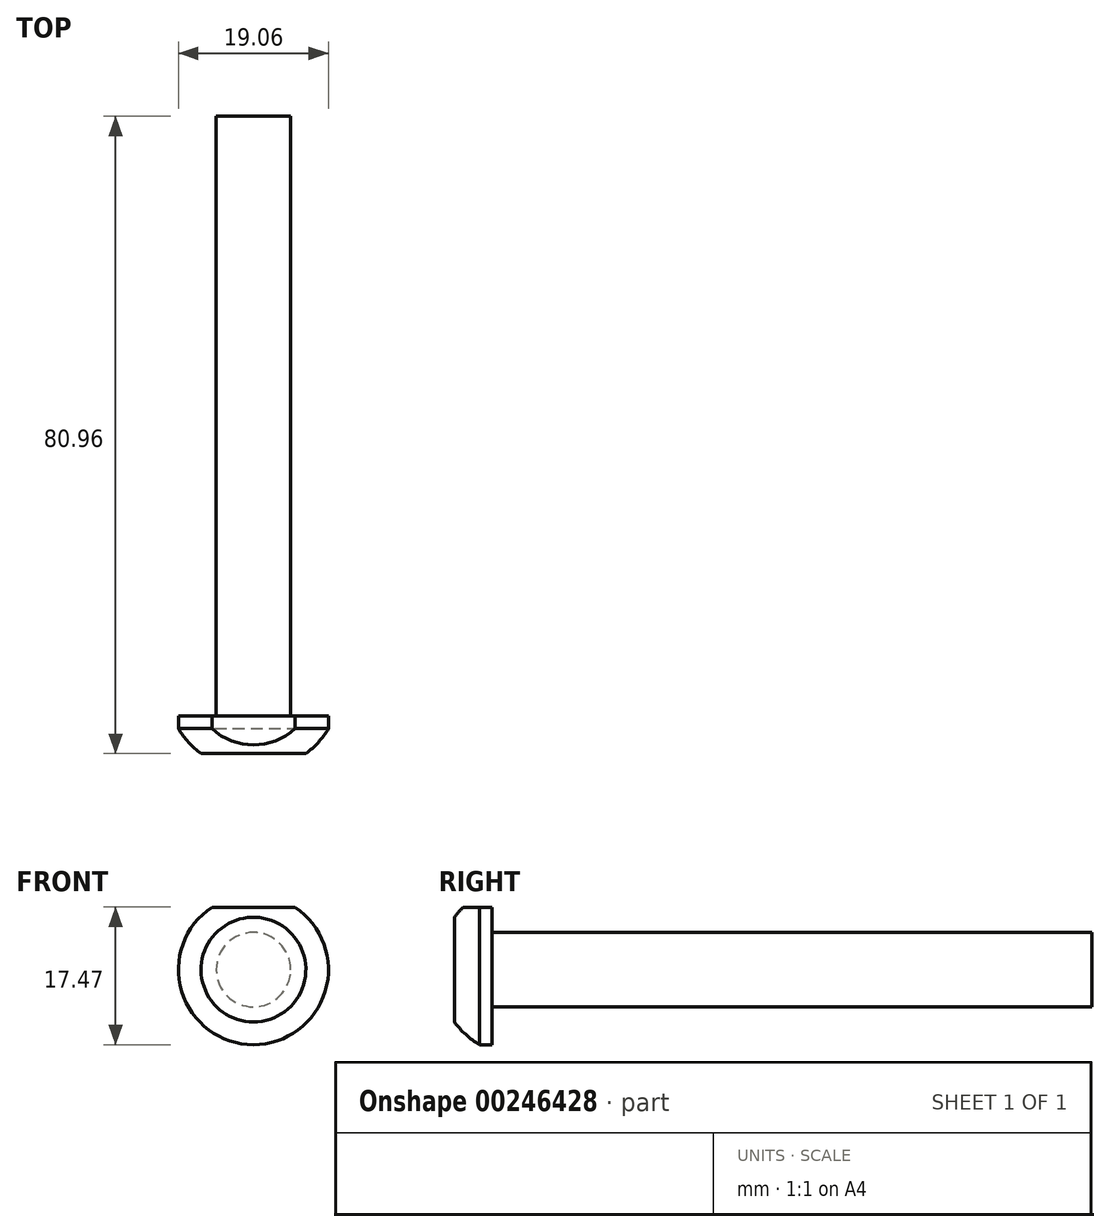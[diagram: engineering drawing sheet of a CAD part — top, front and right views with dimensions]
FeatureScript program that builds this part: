
annotation { "Feature Type Name" : "Feature", "Feature Type Description" : "" }
export const myFeature = defineFeature(function(context is Context, id is Id, definition is map)
    precondition{}
    {
        {
            var Q0;
            Q0=qCreatedBy(makeId("Right.planeOp"),FACE);
            var sketch = newSketch(context, id + "F0", { "sketchPlane" : qUnion([Q0])});
            skLineSegment(sketch, "E0.bottom", {"start": v(0, 0) * mm, "end": v(76.2, 0) * mm});
            skLineSegment(sketch, "E0.top", {"start": v(0, 4.72) * mm, "end": v(76.2, 4.72) * mm});
            skLineSegment(sketch, "E0.left", {"start": v(0, 0) * mm, "end": v(0, 4.72) * mm});
            skLineSegment(sketch, "E0.right", {"start": v(76.2, 0) * mm, "end": v(76.2, 4.72) * mm});
            skLineSegment(sketch, "E1.bottom", {"start": v(0, 0) * mm, "end": v(-4.76, 0) * mm});
            skLineSegment(sketch, "E1.top", {"start": v(0, 9.53) * mm, "end": v(-1.59, 9.53) * mm});
            skLineSegment(sketch, "E1.left", {"start": v(0, 0) * mm, "end": v(0, 9.53) * mm});
            skArc(sketch, "E2", {"start": v(-1.59, 9.52) * mm, "mid": v(-3.31, 8.24) * mm, "end": v(-4.76, 6.66) * mm});
            skLineSegment(sketch, "E3", {"start": v(-4.76, 6.66) * mm, "end": v(-4.76, 0) * mm});
            skSolve(sketch);
        }
        {
            var Q0;
            {var subQ0=sQuery(id+"F0.wireOp",EDGE,"E0.bottom");Q0=makeQuery(id+"F0.imprint","IMPRINT",FACE,{"disambiguationData":[TD([[makeQuery(id+"F0.imprint","IMPRINT",EDGE,{"derivedFrom":subQ0}),1.0]])]});}
            var Q1;
            {var subQ3=sQuery(id+"F0.wireOp",EDGE,"E1.bottom");Q1=makeQuery(id+"F0.imprint","IMPRINT",FACE,{"disambiguationData":[TD([[makeQuery(id+"F0.imprint","IMPRINT",EDGE,{"derivedFrom":subQ3}),-1.0]])]});}
            var Q2;
            Q2=sQuery(id+"F0.wireOp",EDGE,"E0.bottom");
            revolve(context, id + "F1", {"entities" : qUnion([Q0, Q1]), "axis" : qUnion([Q2]), "revolveType" : RevolveType.FULL});
        }
        {
            var Q0;
            Q0=makeQuery(id+"F1.opRevolve","SWEPT_FACE",FACE,{"disambiguationData":[OSD([sQuery(id+"F0.wireOp",EDGE,"E3")])]});
            var sketch = newSketch(context, id + "F2", { "sketchPlane" : qUnion([Q0])});
            skLineSegment(sketch, "E4", {"start": v(0, 0) * mm, "end": v(0, 8.15) * mm});
            skLineSegment(sketch, "E5.bottom", {"start": v(9.86, 11.75) * mm, "end": v(-9.2, 11.75) * mm});
            skLineSegment(sketch, "E5.top", {"start": v(9.86, 7.94) * mm, "end": v(-9.2, 7.94) * mm});
            skLineSegment(sketch, "E5.left", {"start": v(9.86, 11.75) * mm, "end": v(9.86, 7.94) * mm});
            skLineSegment(sketch, "E5.right", {"start": v(-9.2, 11.75) * mm, "end": v(-9.2, 7.94) * mm});
            skSolve(sketch);
        }
        {
            var Q0;
            Q0=makeQuery(id+"F2.imprint","IMPRINT",FACE,{"disambiguationData":[TD([[makeQuery(id+"F2.imprint","IMPRINT",EDGE,{"derivedFrom":sQuery(id+"F2.wireOp",EDGE,"E5.bottom")}),1.0]])]});
            extrude(context, id + "F3", {"entities" : qUnion([Q0]), "operationType" : NewBodyOperationType.REMOVE, "oppositeDirection" : true, "depth" : 4.76 * mm});
        }
    });
